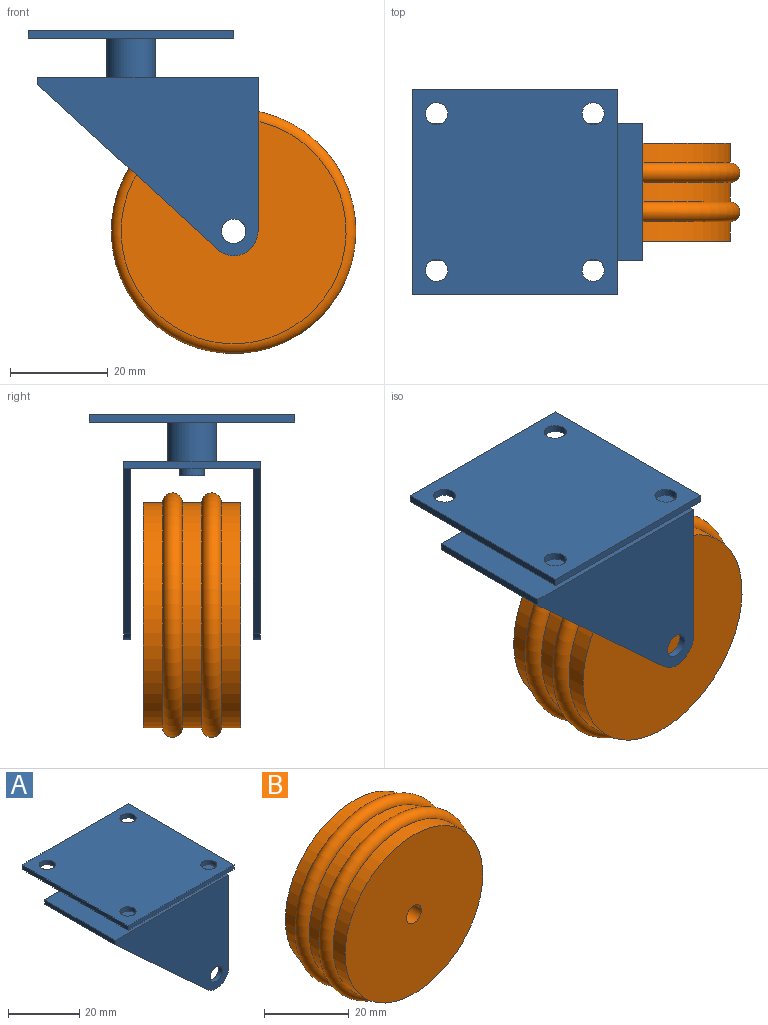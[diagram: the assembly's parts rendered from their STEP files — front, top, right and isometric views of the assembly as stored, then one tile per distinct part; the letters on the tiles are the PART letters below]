
ASSEMBLY  parts=2 mates=2
PART A: 27 faces, bbox 47x42x46 mm
  f0: cylinder r=5mm len=10mm, axis (0,0,-1), area 251.3mm2, adj f14,f25
  f1: plane 36.62x33.68mm, normal (-0.68,0,-0.74), area 74.6mm2, adj f4,f5,f6,f13
  f2: plane 31.5x28mm, normal (1,0,0), area 132mm2, adj f4,f5,f6,f9,f10,f11,f12,f14
  f3: cylinder r=2.5mm len=5mm, axis (0,-1,0), area 23.6mm2, adj f5,f6
  f4: cylinder r=5mm len=8.39mm, axis (0,-1,0), area 17.4mm2, adj f1,f2,f5,f6
  f5: plane 45x36.5mm, normal (0,1,0), area 951.2mm2, adj f1,f2,f3,f4,f13,f14
  f6: plane 45x35mm, normal (0,-1,0), area 883.7mm2, adj f1,f2,f3,f4,f12
  f7: plane 36.62x33.68mm, normal (-0.68,0,-0.74), area 74.6mm2, adj f9,f10,f11,f13
  f8: cylinder r=2.5mm len=5mm, axis (0,1,0), area 23.6mm2, adj f10,f11
  f9: cylinder r=5mm len=8.39mm, axis (0,1,0), area 17.4mm2, adj f2,f7,f10,f11
  f10: plane 45x36.5mm, normal (0,-1,0), area 951.2mm2, adj f2,f7,f8,f9,f13,f14
  f11: plane 45x35mm, normal (0,1,0), area 883.7mm2, adj f2,f7,f8,f9,f12
  f12: plane 45x25mm, normal (0,0,-1), area 1105.4mm2, adj f2,f6,f11,f13,f16
  f13: plane 28x1.5mm, normal (-1,0,0), area 42mm2, adj f1,f5,f7,f10,f12,f14
  f14: plane 45x28mm, normal (0,0,1), area 1181.5mm2, adj f0,f2,f5,f10,f13
  f15: plane 5x5mm, normal (0,0,-1), area 19.6mm2, adj f16
  f16: cylinder r=2.5mm len=5mm, axis (0,0,1), area 23.6mm2, adj f12,f15
  f17: plane 42x1.5mm, normal (-1,0,0), area 63mm2, adj f18,f20,f25,f26
  f18: plane 42x1.5mm, normal (0,-1,0), area 63mm2, adj f17,f19,f25,f26
  f19: plane 42x1.5mm, normal (1,0,0), area 63mm2, adj f18,f20,f25,f26
  f20: plane 42x1.5mm, normal (0,1,0), area 63mm2, adj f17,f19,f25,f26
  f21: cylinder r=2.25mm len=4.5mm, axis (0,0,1), area 21.2mm2, adj f25,f26
  f22: cylinder r=2.25mm len=4.5mm, axis (0,0,1), area 21.2mm2, adj f25,f26
  f23: cylinder r=2.25mm len=4.5mm, axis (0,0,1), area 21.2mm2, adj f25,f26
  f24: cylinder r=2.25mm len=4.5mm, axis (0,0,1), area 21.2mm2, adj f25,f26
  f25: plane 42x42mm, normal (0,0,-1), area 1621.8mm2, adj f0,f17,f18,f19,f20,f21,f22,f23
  f26: plane 42x42mm, normal (0,0,1), area 1700.4mm2, adj f17,f18,f19,f20,f21,f22,f23,f24
PART B: 8 faces, bbox 54.1x20x54.1 mm
  f0: torus R=23mm, axis (0,1,0), area 958.3mm2, adj f1,f7
  f1: cylinder r=23mm len=46mm, axis (0,1,0), area 578.1mm2, adj f0,f2
  f2: plane 46x46mm, normal (0,-1,0), area 1642.3mm2, adj f1,f3
  f3: cylinder r=2.5mm len=20mm, axis (0,1,0), area 314.2mm2, adj f2,f4
  f4: plane 46x46mm, normal (0,1,0), area 1642.3mm2, adj f3,f5
  f5: cylinder r=23mm len=46mm, axis (0,1,0), area 578.1mm2, adj f4,f6
  f6: torus R=23mm, axis (0,1,0), area 958.3mm2, adj f5,f7
  f7: cylinder r=23mm len=46mm, axis (0,1,0), area 578.1mm2, adj f0,f6
PLACE A at identity
PLACE B at identity
MATE planar B.f0 <-> A.f3  axis (0,-1,0) through (0,-10,0)mm
MATE cylindrical B.f0 <-> A.f3  axis (0,-1,0) through (0,-10,0)mm
